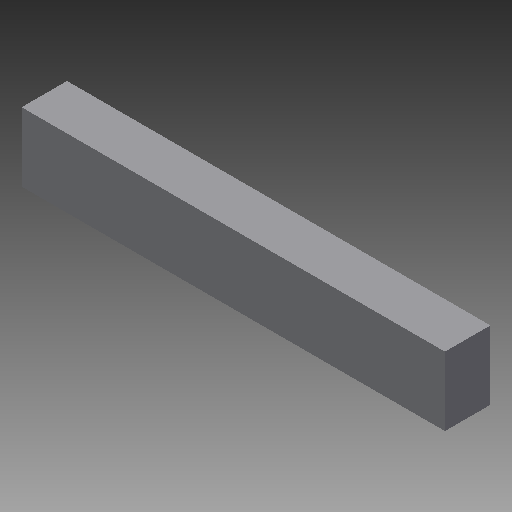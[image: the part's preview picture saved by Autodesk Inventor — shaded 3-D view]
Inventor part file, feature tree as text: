
AUTODESK INVENTOR PART (.ipt)
format: ipt  version: 2017 (Build 210142000, 142)  size: 74,240 bytes
history: native  units: in
note: dims shown in document units (in); Inventor stores cm internally (conversion verified against a paired STEP export)
features: extrude x1, sketch x1
ambient origin geometry x8: Origin, YZ Plane, XZ Plane, XY Plane, X Axis, Y Axis, Z Axis, Center Point
bodies: Solid1 (feature_tree)
feature tree (2):
  extrude  "Extrusion1"  Depth=0.217in
  sketch  "Sketch1"  dims[d0=2.02in d1=0.217in d2=0.328in d3=0.0in]
